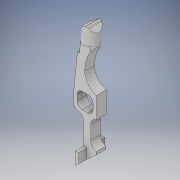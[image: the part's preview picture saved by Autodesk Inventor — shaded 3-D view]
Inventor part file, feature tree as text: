
AUTODESK INVENTOR PART (.ipt)
format: ipt  version: 2018.3 (Build 223284000, 284)  size: 255,488 bytes
history: native  units: in
note: dims shown in document units (in); Inventor stores cm internally (conversion verified against a paired STEP export)
features: extrude x7, sketch x3, revolve x1, plane x1
ambient origin geometry x8: Origin, YZ Plane, XZ Plane, XY Plane, X Axis, Y Axis, Z Axis, Center Point
bodies: Solid1 (feature_tree)
feature tree (12):
  sketch  "Sketch1"  dims[d0=0.174in d1=0.174in]
  extrude  "Extrusion1"  Depth=0.174in
  revolve  "Revolution1"  [1 undecoded]
  extrude  "Extrusion2"  Depth=0.285in
  extrude  "Extrusion3"  Depth=0.004in
  extrude  "Extrusion4"  Depth=0.06in
  plane  "Work Plane1"
  extrude  "Extrusion5"  Depth=0.08in
  extrude  "Extrusion6"  Depth=0.08in
  extrude  "Extrusion7"  Depth=0.285in
  sketch  "Sketch3"  dims[d2=0.055in d3=0.19in]
  sketch  "Sketch4"  dims[d4=0.038in d5=1.1956in d6=0.004in d7=0.06in d8=0.08in d9=0.08in d10=0.03in d11=0.3298in d12=0.476in d13=0.34in d14=0.205in d15=0.079in d16=0.78in d17=0.337in d19=0.035in d20=0.06in d21=0.05in d22=0.109in d23=0.2886in d24=0.3023in d25=0.03in d26=0.015in d27=0.739in d28=0.21in d29=0.038in d30=0.155in d32=0.051in d33=0.0775in d34=0.312in d35=0.0775in d36=90.0deg d37=0.107in d38=0.0in d39=0.47in d40=0.0535in d41=0.2945in d42=0.0in d43=0.107in d44=0.0in d45=0.107in d46=0.0in d47=0.0in d48=0.312in d49=0.0in d50=0.312in d51=0.0in d52=0.285in d53=0.0in]
note: 1 required parameter value undecoded (feature->parameter linkage not recoverable at this tier; creation-order binding heuristic only, values carry confidence <= 0.55)
